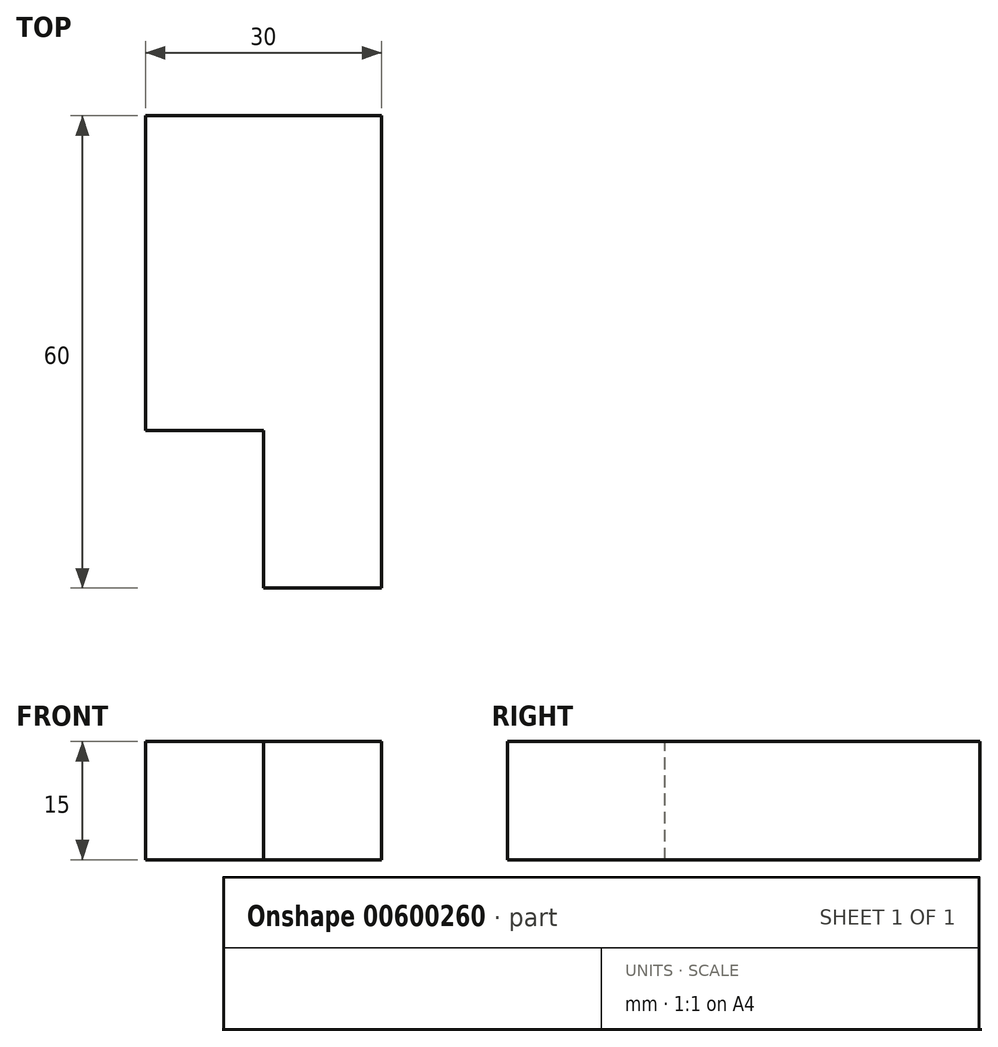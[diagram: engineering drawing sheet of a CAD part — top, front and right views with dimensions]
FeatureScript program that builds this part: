
annotation { "Feature Type Name" : "Feature", "Feature Type Description" : "" }
export const myFeature = defineFeature(function(context is Context, id is Id, definition is map)
    precondition{}
    {
        {
            var Q0;
            Q0=qCreatedBy(makeId("Right.planeOp"),FACE);
            var sketch = newSketch(context, id + "F0", { "sketchPlane" : qUnion([Q0])});
            skLineSegment(sketch, "E0.bottom", {"start": v(0, 0) * mm, "end": v(60, 0) * mm});
            skLineSegment(sketch, "E0.top", {"start": v(0, 15) * mm, "end": v(60, 15) * mm});
            skLineSegment(sketch, "E0.left", {"start": v(0, 0) * mm, "end": v(0, 15) * mm});
            skLineSegment(sketch, "E0.right", {"start": v(60, 0) * mm, "end": v(60, 15) * mm});
            skSolve(sketch);
        }
        {
            var Q0;
            Q0 = qSketchRegion(id + "F0", true);
            extrude(context, id + "F1", {"entities" : qUnion([Q0]), "depth" : 30 * mm, "offsetDistance" : 25 * mm});
        }
        {
            var Q0;
            Q0=makeQuery(id+"F1.opExtrude","SWEPT_FACE",FACE,{"disambiguationData":[OSD([sQuery(id+"F0.wireOp",EDGE,"E0.top")])]});
            var sketch = newSketch(context, id + "F2", { "sketchPlane" : qUnion([Q0])});
            skLineSegment(sketch, "E1.bottom", {"start": v(0, 0) * mm, "end": v(15, 0) * mm});
            skLineSegment(sketch, "E1.top", {"start": v(0, 20) * mm, "end": v(15, 20) * mm});
            skLineSegment(sketch, "E1.left", {"start": v(0, 0) * mm, "end": v(0, 20) * mm});
            skLineSegment(sketch, "E1.right", {"start": v(15, 0) * mm, "end": v(15, 20) * mm});
            skSolve(sketch);
        }
        {
            var Q0;
            Q0 = qSketchRegion(id + "F2", true);
            extrude(context, id + "F3", {"entities" : qUnion([Q0]), "operationType" : NewBodyOperationType.REMOVE, "oppositeDirection" : true, "depth" : 25 * mm, "offsetDistance" : 25 * mm});
        }
    });
